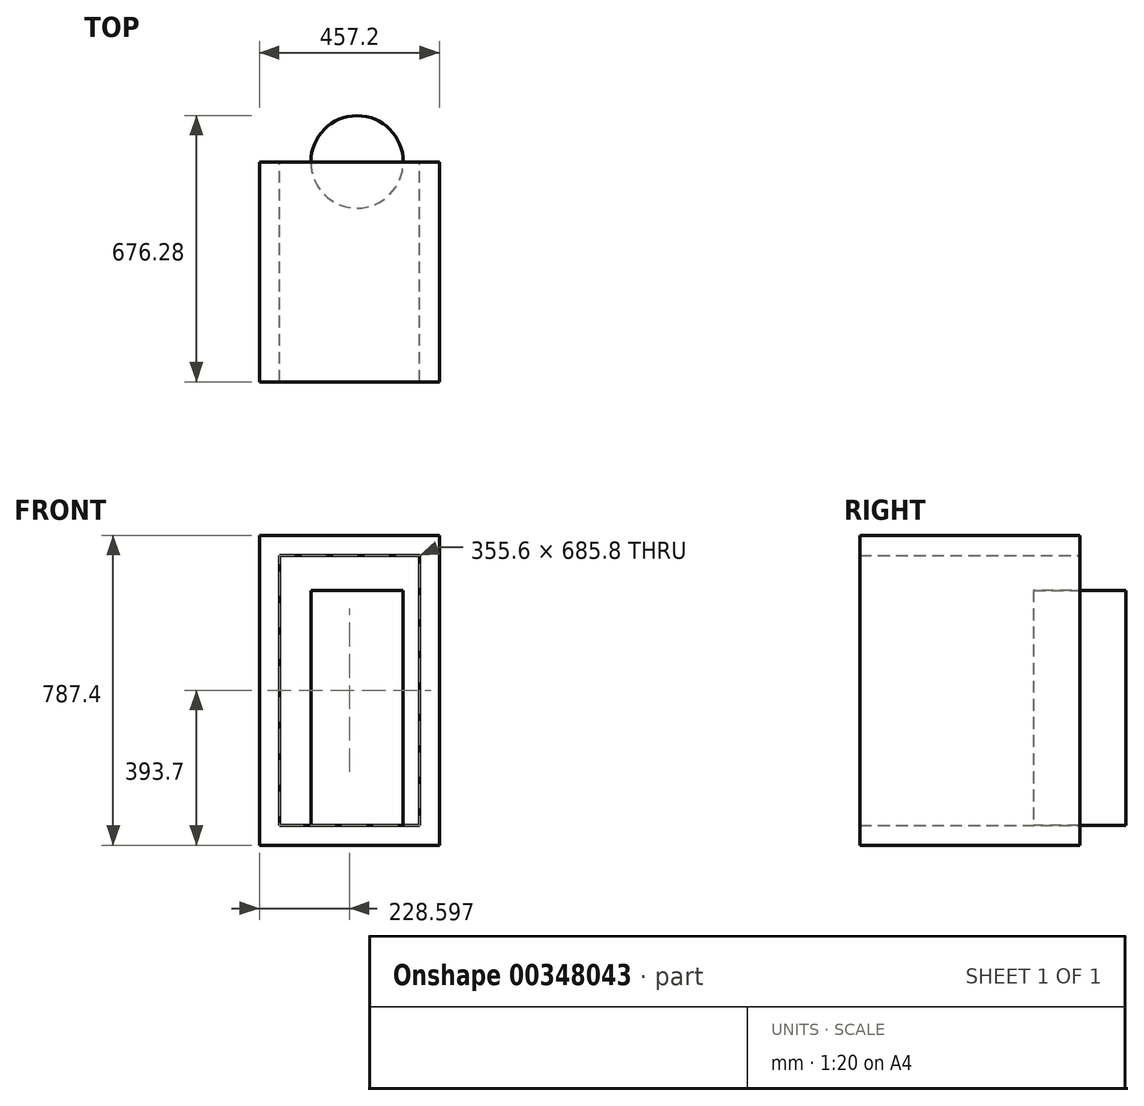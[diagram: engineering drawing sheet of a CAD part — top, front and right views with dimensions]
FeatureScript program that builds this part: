
annotation { "Feature Type Name" : "Feature", "Feature Type Description" : "" }
export const myFeature = defineFeature(function(context is Context, id is Id, definition is map)
    precondition{}
    {
        {
            var Q0;
            Q0=qCreatedBy(makeId("Top.planeOp"),FACE);
            var sketch = newSketch(context, id + "F0", { "sketchPlane" : qUnion([Q0])});
            skCircle(sketch, "E0", {"center": v(0, 0) * mm, "radius": 117.48 * mm});
            skSolve(sketch);
        }
        {
            var Q0;
            Q0 = qSketchRegion(id + "F0", true);
            extrude(context, id + "F1", {"entities" : qUnion([Q0]), "depth" : 596.9 * mm});
        }
        {
            var Q0;
            Q0=qCreatedBy(makeId("Front.planeOp"),FACE);
            var sketch = newSketch(context, id + "F2", { "sketchPlane" : qUnion([Q0])});
            skLineSegment(sketch, "E1", {"start": v(158.19, 0) * mm, "end": v(158.19, 685.8) * mm});
            skLineSegment(sketch, "E2", {"start": v(158.19, 685.8) * mm, "end": v(-197.41, 685.8) * mm});
            skLineSegment(sketch, "E3", {"start": v(-197.41, 685.8) * mm, "end": v(-197.41, 0) * mm});
            skLineSegment(sketch, "E4", {"start": v(-197.41, 0) * mm, "end": v(158.19, 0) * mm});
            skLineSegment(sketch, "E5", {"start": v(208.99, 0) * mm, "end": v(208.99, 736.6) * mm});
            skLineSegment(sketch, "E6", {"start": v(208.99, 736.6) * mm, "end": v(-248.21, 736.6) * mm});
            skLineSegment(sketch, "E7", {"start": v(-248.21, 736.6) * mm, "end": v(-248.21, -50.8) * mm});
            skLineSegment(sketch, "E8", {"start": v(-248.21, -50.8) * mm, "end": v(208.99, -50.8) * mm});
            skLineSegment(sketch, "E9", {"start": v(208.99, 0) * mm, "end": v(208.99, -50.8) * mm});
            skSolve(sketch);
        }
        {
            var Q0;
            Q0=makeQuery(id+"F2.imprint","IMPRINT",FACE,{"disambiguationData":[TD([[makeQuery(id+"F2.imprint","IMPRINT",EDGE,{"derivedFrom":sQuery(id+"F2.wireOp",EDGE,"E1")}),-1.0]])]});
            extrude(context, id + "F3", {"entities" : qUnion([Q0]), "operationType" : NewBodyOperationType.ADD, "depth" : 558.8 * mm});
        }
    });
